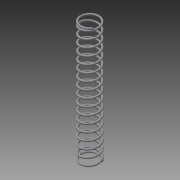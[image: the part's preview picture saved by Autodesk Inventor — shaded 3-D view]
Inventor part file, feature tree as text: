
AUTODESK INVENTOR PART (.ipt)
format: ipt  version: 2014 SP1 (Build 180222100, 222)  size: 649,216 bytes
history: native  units: in
note: dims shown in document units (in); Inventor stores cm internally (conversion verified against a paired STEP export)
features: sketch x3, revolve x2, projected_geometry x2, other x1, helix x1
ambient origin geometry x8: Origin, YZ Plane, XZ Plane, XY Plane, X Axis, Y Axis, Z Axis, Center Point
bodies: Solid1 (feature_tree)
feature tree (9):
  other  "Recoil Spring"
  helix  "Coil1"  [1 undecoded]
  revolve  "Revolution1"  [1 undecoded]
  revolve  "Revolution2"  [1 undecoded]
  sketch  "Sketch1"  dims[d1=0.45in d3=2.7746in]
  sketch  "Sketch2"  dims[d4=2.7326in d5=1.0in d6=2.7326in]
  projected_geometry  "Projected Loop1"
  sketch  "Sketch3"  dims[d7=6.2992in d8=0.0in d9=90.0deg d10=90.0deg d11=90.0deg d12=90.0deg d13=150.0deg d14=150.0deg]
  projected_geometry  "Projected Loop2"
note: 3 required parameter values undecoded (feature->parameter linkage not recoverable at this tier; creation-order binding heuristic only, values carry confidence <= 0.55)